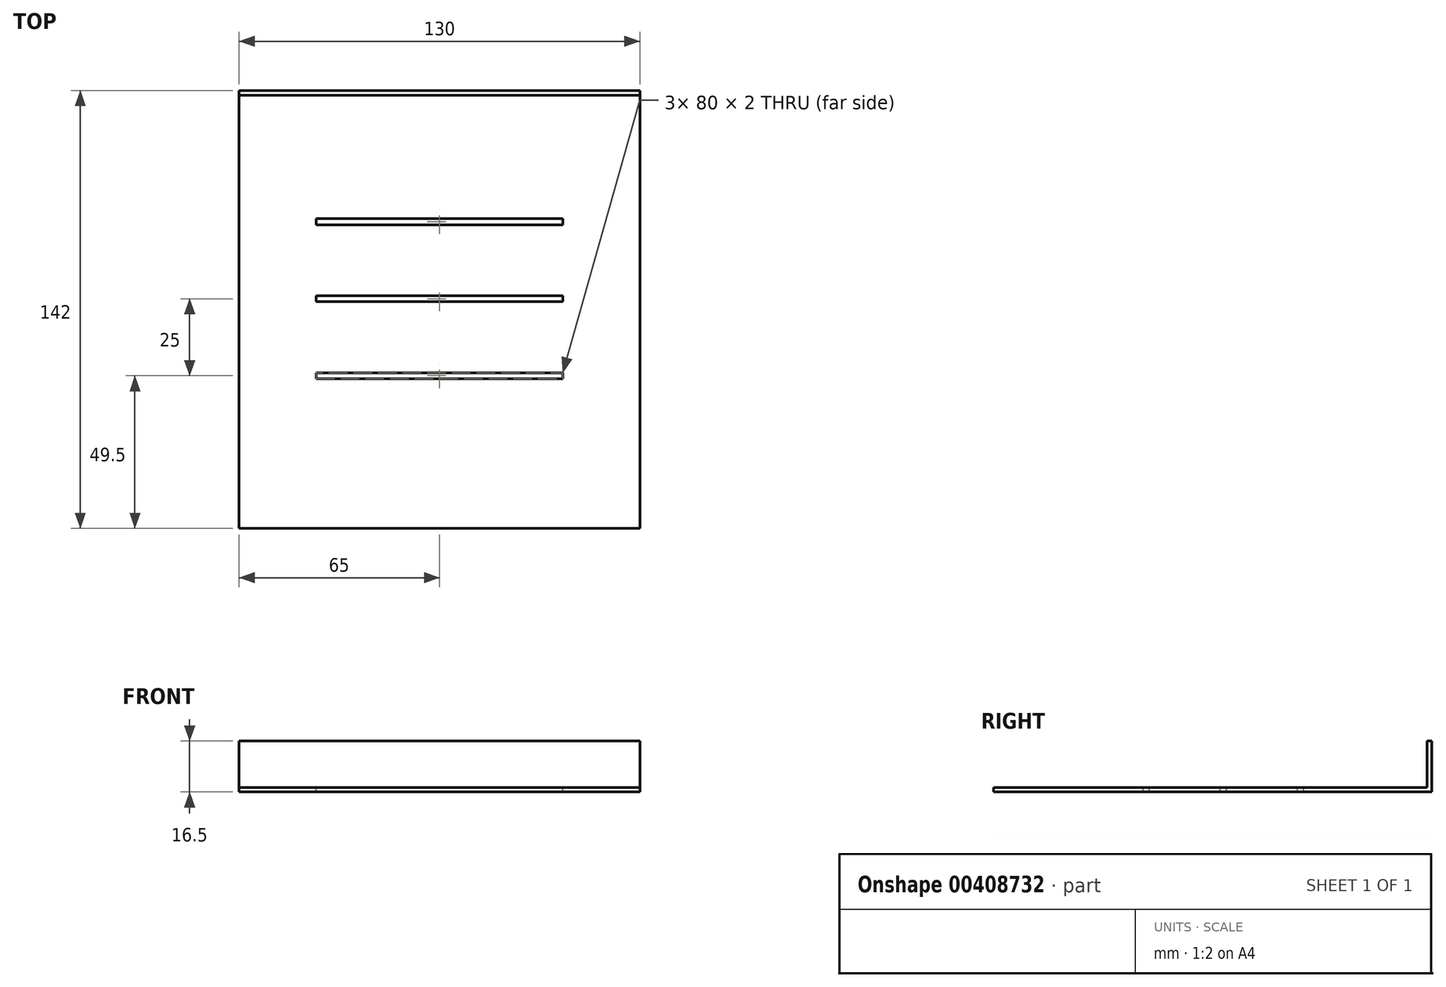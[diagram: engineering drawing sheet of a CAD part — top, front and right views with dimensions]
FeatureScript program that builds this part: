
annotation { "Feature Type Name" : "Feature", "Feature Type Description" : "" }
export const myFeature = defineFeature(function(context is Context, id is Id, definition is map)
    precondition{}
    {
        {
            assignVariable(context, id + "F0", {"name" : "minThickness", "anyValue" : 1.5});
        }
        {
            assignVariable(context, id + "F1", {"name" : "lipSize", "anyValue" : 15});
        }
        {
            var Q0;
            Q0=qCreatedBy(makeId("Top.planeOp"),FACE);
            var sketch = newSketch(context, id + "F2", { "sketchPlane" : qUnion([Q0])});
            skLineSegment(sketch, "E0.bottom", {"start": v(-65, 71) * mm, "end": v(65, 71) * mm});
            skLineSegment(sketch, "E0.top", {"start": v(-65, -71) * mm, "end": v(65, -71) * mm});
            skLineSegment(sketch, "E0.left", {"start": v(-65, 71) * mm, "end": v(-65, -71) * mm});
            skLineSegment(sketch, "E0.right", {"start": v(65, 71) * mm, "end": v(65, -71) * mm});
            skPoint(sketch, "E0.middle", {"position": v(0, 0) * mm});
            skLineSegment(sketch, "E1", {"start": v(-65, 69.5) * mm, "end": v(65, 69.5) * mm});
            skSolve(sketch);
        }
        {
            var Q0;
            {var subQ0=sQuery(id+"F2.wireOp",EDGE,"E0.top");Q0=makeQuery(id+"F2.imprint","IMPRINT",FACE,{"disambiguationData":[TD([[makeQuery(id+"F2.imprint","IMPRINT",EDGE,{"derivedFrom":subQ0}),1.0]])]});}
            extrude(context, id + "F3", {"entities" : qUnion([Q0]), "depth" : (getVariable(context, 'minThickness')) * mm, "offsetDistance" : 25 * mm});
        }
        {
            var Q0;
            {var subQ0=sQuery(id+"F2.wireOp",EDGE,"E0.bottom");Q0=makeQuery(id+"F2.imprint","IMPRINT",FACE,{"disambiguationData":[TD([[makeQuery(id+"F2.imprint","IMPRINT",EDGE,{"derivedFrom":subQ0}),-1.0]])]});}
            extrude(context, id + "F4", {"entities" : qUnion([Q0]), "operationType" : NewBodyOperationType.ADD, "depth" : (getVariable(context, 'minThickness') + getVariable(context, 'lipSize')) * mm, "offsetDistance" : 25 * mm});
        }
        {
            var Q0;
            Q0=makeQuery(id+"F3.opExtrude","CAP_FACE",FACE,{"disambiguationData":[OSD([sQuery(id+"F2.wireOp",EDGE,"E0.top"),sQuery(id+"F2.wireOp",EDGE,"E0.left"),sQuery(id+"F2.wireOp",EDGE,"E0.right"),sQuery(id+"F2.wireOp",EDGE,"E1")])],"isStart":false});
            var sketch = newSketch(context, id + "F5", { "sketchPlane" : qUnion([Q0])});
            skLineSegment(sketch, "E2.bottom", {"start": v(-40, 29.5) * mm, "end": v(40, 29.5) * mm});
            skLineSegment(sketch, "E2.top", {"start": v(-40, 27.5) * mm, "end": v(40, 27.5) * mm});
            skLineSegment(sketch, "E2.left", {"start": v(-40, 29.5) * mm, "end": v(-40, 27.5) * mm});
            skLineSegment(sketch, "E2.right", {"start": v(40, 29.5) * mm, "end": v(40, 27.5) * mm});
            skPoint(sketch, "E2.middle", {"position": v(0, 28.5) * mm});
            skLineSegment(sketch, "E3.0.1.0", {"start": v(-40, 4.5) * mm, "end": v(40, 4.5) * mm});
            skLineSegment(sketch, "E3.0.1.1", {"start": v(-40, 2.5) * mm, "end": v(40, 2.5) * mm});
            skLineSegment(sketch, "E3.0.1.2", {"start": v(-40, 4.5) * mm, "end": v(-40, 2.5) * mm});
            skLineSegment(sketch, "E3.0.1.3", {"start": v(40, 4.5) * mm, "end": v(40, 2.5) * mm});
            skLineSegment(sketch, "E3.0.2.0", {"start": v(-40, -20.5) * mm, "end": v(40, -20.5) * mm});
            skLineSegment(sketch, "E3.0.2.1", {"start": v(-40, -22.5) * mm, "end": v(40, -22.5) * mm});
            skLineSegment(sketch, "E3.0.2.2", {"start": v(-40, -20.5) * mm, "end": v(-40, -22.5) * mm});
            skLineSegment(sketch, "E3.0.2.3", {"start": v(40, -20.5) * mm, "end": v(40, -22.5) * mm});
            skLineSegment(sketch, "E3.direction1", {"start": v(-40, 29.5) * mm, "end": v(-20.6, 29.5) * mm, "construction": true});
            skLineSegment(sketch, "E3.direction2", {"start": v(-40, 29.5) * mm, "end": v(-40, 4.5) * mm, "construction": true});
            skSolve(sketch);
        }
        {
            var Q0;
            Q0 = qSketchRegion(id + "F5", true);
            extrude(context, id + "F6", {"entities" : qUnion([Q0]), "operationType" : NewBodyOperationType.REMOVE, "endBound" : BoundingType.THROUGH_ALL, "oppositeDirection" : true, "depth" : 25 * mm, "offsetDistance" : 25 * mm});
        }
    });
